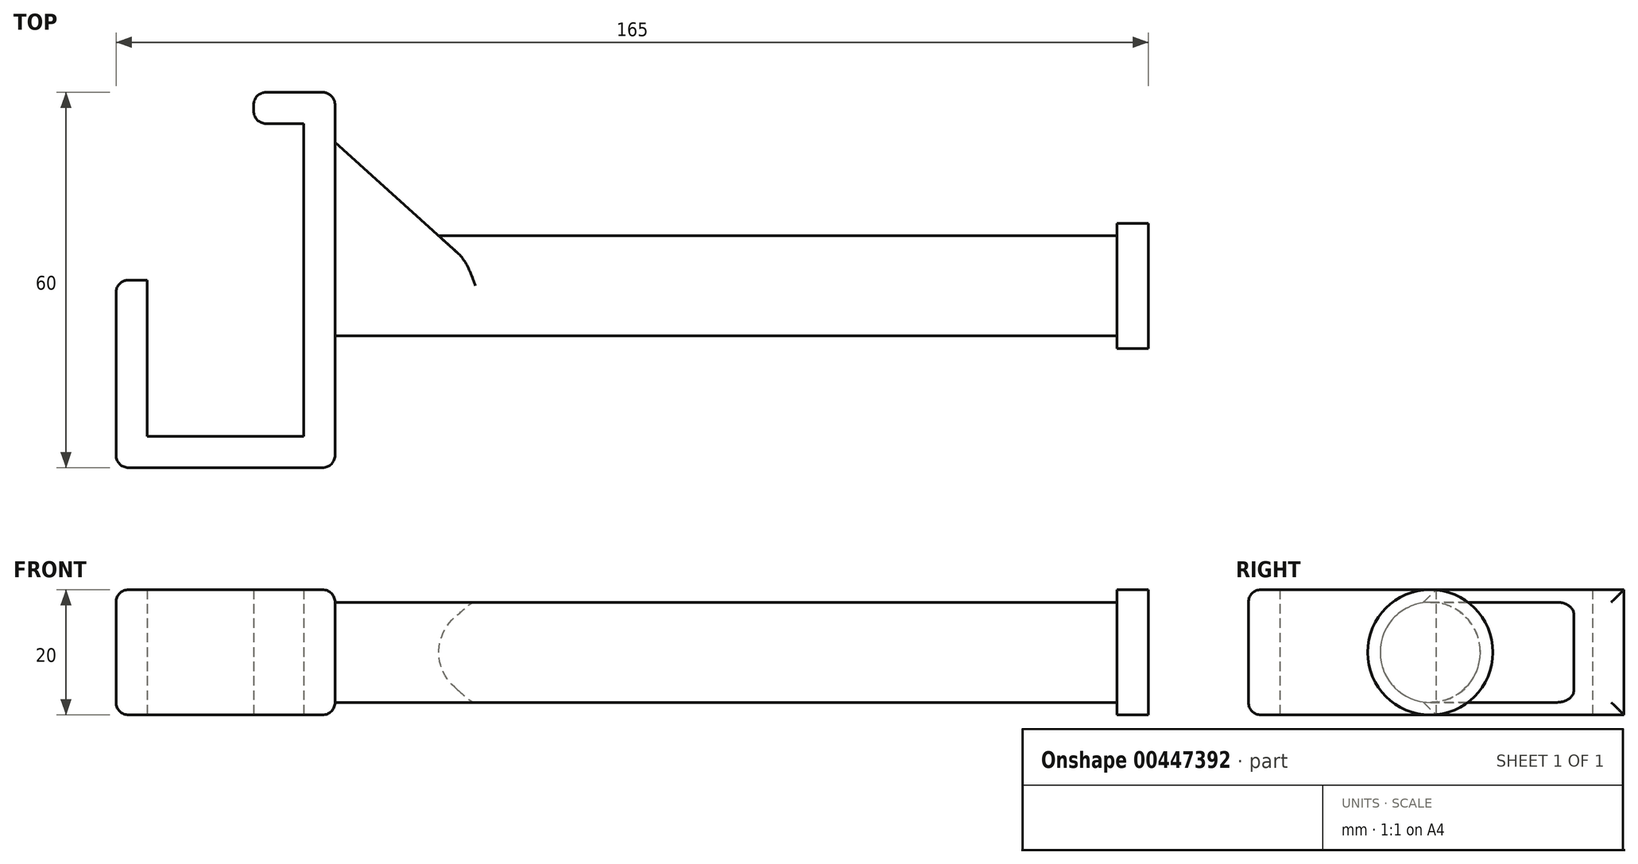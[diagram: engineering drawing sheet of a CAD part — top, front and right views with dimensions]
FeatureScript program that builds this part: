
annotation { "Feature Type Name" : "Feature", "Feature Type Description" : "" }
export const myFeature = defineFeature(function(context is Context, id is Id, definition is map)
    precondition{}
    {
        {
            var Q0;
            Q0=qCreatedBy(makeId("Top.planeOp"),FACE);
            var sketch = newSketch(context, id + "F0", { "sketchPlane" : qUnion([Q0])});
            skLineSegment(sketch, "E0", {"start": v(-33.28, 0.94) * mm, "end": v(-33.28, -24.06) * mm});
            skLineSegment(sketch, "E1", {"start": v(-33.28, -24.06) * mm, "end": v(-8.28, -24.06) * mm});
            skLineSegment(sketch, "E2", {"start": v(-8.28, -24.06) * mm, "end": v(-8.28, 25.94) * mm});
            skLineSegment(sketch, "E3", {"start": v(-8.28, 25.94) * mm, "end": v(-16.28, 25.94) * mm});
            skLineSegment(sketch, "E4.0", {"start": v(-3.28, 30.94) * mm, "end": v(-16.28, 30.94) * mm});
            skLineSegment(sketch, "E4.1", {"start": v(-3.28, -29.06) * mm, "end": v(-3.28, 30.94) * mm});
            skLineSegment(sketch, "E4.2", {"start": v(-38.28, -29.06) * mm, "end": v(-3.28, -29.06) * mm});
            skLineSegment(sketch, "E4.3", {"start": v(-38.28, 0.94) * mm, "end": v(-38.28, -29.06) * mm});
            skLineSegment(sketch, "E5", {"start": v(-16.28, 30.94) * mm, "end": v(-16.28, 25.94) * mm});
            skLineSegment(sketch, "E6", {"start": v(-38.28, 0.94) * mm, "end": v(-33.28, 0.94) * mm});
            skSolve(sketch);
        }
        {
            var Q0;
            Q0=makeQuery(id+"F0.imprint","IMPRINT",FACE,{"disambiguationData":[TD([[makeQuery(id+"F0.imprint","IMPRINT",EDGE,{"derivedFrom":sQuery(id+"F0.wireOp",EDGE,"E0")}),-1.0]])]});
            extrude(context, id + "F1", {"entities" : qUnion([Q0]), "endBound" : BoundingType.SYMMETRIC, "depth" : 20 * mm});
        }
        {
            var Q0;
            Q0=makeQuery(id+"F1.opExtrude","SWEPT_FACE",FACE,{"disambiguationData":[OSD([sQuery(id+"F0.wireOp",EDGE,"E4.1")])]});
            var sketch = newSketch(context, id + "F2", { "sketchPlane" : qUnion([Q0])});
            skCircle(sketch, "E7", {"center": v(0, 0) * mm, "radius": 8 * mm});
            skSolve(sketch);
        }
        {
            var Q0;
            {var subQ0=sQuery(id+"F2.wireOp",EDGE,"E7");var subQ1=sQuery(id+"F0.wireOp",EDGE,"E4.1");var subQ2=makeQuery(id+"F2.imprint","INTERSECT",VERTEX,{"derivedFrom":[makeQuery(id+"F1.opExtrude","CAP_EDGE",EDGE,{"disambiguationData":[OSD([subQ1])],"isStart":true}),subQ0]});Q0=makeQuery(id+"F2.imprint","IMPRINT",FACE,{"disambiguationData":[TD([[makeQuery(id+"F2.imprint","IMPRINT",EDGE,{"disambiguationData":[TD([[subQ2,1.0]])],"derivedFrom":subQ0}),1.0]])]});}
            extrude(context, id + "F3", {"entities" : qUnion([Q0]), "operationType" : NewBodyOperationType.ADD, "depth" : 125 * mm});
        }
        {
            var Q0;
            Q0=makeQuery(id+"F3.opExtrude","CAP_FACE",FACE,{"disambiguationData":[OSD([sQuery(id+"F2.wireOp",EDGE,"E7")])],"isStart":false});
            var sketch = newSketch(context, id + "F4", { "sketchPlane" : qUnion([Q0])});
            skCircle(sketch, "E8", {"center": v(0, 0) * mm, "radius": 10 * mm});
            skSolve(sketch);
        }
        {
            var Q0;
            Q0=makeQuery(id+"F4.imprint","IMPRINT",FACE,{"disambiguationData":[TD([[makeQuery(id+"F4.imprint","IMPRINT",EDGE,{"derivedFrom":sQuery(id+"F4.wireOp",EDGE,"E8")}),1.0]])]});
            var Q1;
            Q1=makeQuery(id+"F4.imprint","IMPRINT",FACE,{"disambiguationData":[TD([[makeQuery(id+"F4.imprint","IMPRINT",EDGE,{"derivedFrom":makeQuery(id+"F3.opExtrude","CAP_EDGE",EDGE,{"disambiguationData":[OSD([sQuery(id+"F2.wireOp",EDGE,"E7")])],"isStart":false})}),1.0]])]});
            extrude(context, id + "F5", {"entities" : qUnion([Q0, Q1]), "operationType" : NewBodyOperationType.ADD, "depth" : 5 * mm});
        }
        {
            var Q0;
            Q0=qCreatedBy(makeId("Top.planeOp"),FACE);
            var sketch = newSketch(context, id + "F6", { "sketchPlane" : qUnion([Q0])});
            skLineSegment(sketch, "E9", {"start": v(-4.72, 24.28) * mm, "end": v(22.16, 0) * mm});
            skLineSegment(sketch, "E10", {"start": v(22.16, 0) * mm, "end": v(-7.47, 0) * mm});
            skLineSegment(sketch, "E11", {"start": v(-7.47, 0) * mm, "end": v(-4.72, 24.28) * mm});
            skSolve(sketch);
        }
        {
            var Q0;
            Q0=makeQuery(id+"F6.imprint","IMPRINT",FACE,{"disambiguationData":[TD([[makeQuery(id+"F6.imprint","IMPRINT",EDGE,{"derivedFrom":sQuery(id+"F6.wireOp",EDGE,"E9")}),-1.0]])]});
            extrude(context, id + "F7", {"entities" : qUnion([Q0]), "operationType" : NewBodyOperationType.ADD, "endBound" : BoundingType.SYMMETRIC, "depth" : 16 * mm});
        }
        {
            var Q0;
            Q0=makeQuery(id+"F7.opExtrude","CAP_EDGE",EDGE,{"disambiguationData":[OSD([sQuery(id+"F6.wireOp",EDGE,"E9")])],"isStart":false});
            var Q1;
            Q1=makeQuery(id+"F7.opExtrude","CAP_EDGE",EDGE,{"disambiguationData":[OSD([sQuery(id+"F6.wireOp",EDGE,"E9")])],"isStart":true});
            fillet(context, id + "F8", {"entities" : qUnion([Q0, Q1]), "radius" : 2 * mm, "tangentPropagation" : true, "allowEdgeOverflow" : false});
        }
        {
            var Q0;
            Q0=makeQuery(id+"F1.opExtrude","CAP_EDGE",EDGE,{"disambiguationData":[OSD([sQuery(id+"F0.wireOp",EDGE,"E4.1")])],"isStart":false});
            var Q1;
            Q1=makeQuery(id+"F1.opExtrude","CAP_EDGE",EDGE,{"disambiguationData":[OSD([sQuery(id+"F0.wireOp",EDGE,"E4.1")])],"isStart":true});
            var Q2;
            Q2=makeQuery(id+"F1.opExtrude","CAP_EDGE",EDGE,{"disambiguationData":[OSD([sQuery(id+"F0.wireOp",EDGE,"E4.2")])],"isStart":false});
            var Q3;
            Q3=makeQuery(id+"F1.opExtrude","CAP_EDGE",EDGE,{"disambiguationData":[OSD([sQuery(id+"F0.wireOp",EDGE,"E4.2")])],"isStart":true});
            var Q4;
            Q4=makeQuery(id+"F1.opExtrude","CAP_EDGE",EDGE,{"disambiguationData":[OSD([sQuery(id+"F0.wireOp",EDGE,"E4.3")])],"isStart":false});
            var Q5;
            Q5=makeQuery(id+"F1.opExtrude","CAP_EDGE",EDGE,{"disambiguationData":[OSD([sQuery(id+"F0.wireOp",EDGE,"E4.3")])],"isStart":true});
            var Q6;
            Q6=makeQuery(id+"F1.opExtrude","SWEPT_EDGE",EDGE,{"disambiguationData":[OSD([sQuery(id+"F0.wireOp",EDGE,"E4.2"),sQuery(id+"F0.wireOp",EDGE,"E4.3")])]});
            var Q7;
            Q7=makeQuery(id+"F1.opExtrude","SWEPT_EDGE",EDGE,{"disambiguationData":[OSD([sQuery(id+"F0.wireOp",EDGE,"E4.3"),sQuery(id+"F0.wireOp",EDGE,"E6")])]});
            var Q8;
            Q8=makeQuery(id+"F1.opExtrude","SWEPT_EDGE",EDGE,{"disambiguationData":[OSD([sQuery(id+"F0.wireOp",EDGE,"E4.1"),sQuery(id+"F0.wireOp",EDGE,"E4.2")])]});
            var Q9;
            Q9=makeQuery(id+"F1.opExtrude","SWEPT_EDGE",EDGE,{"disambiguationData":[OSD([sQuery(id+"F0.wireOp",EDGE,"E4.0"),sQuery(id+"F0.wireOp",EDGE,"E4.1")])]});
            var Q10;
            Q10=makeQuery(id+"F1.opExtrude","SWEPT_EDGE",EDGE,{"disambiguationData":[OSD([sQuery(id+"F0.wireOp",EDGE,"E4.0"),sQuery(id+"F0.wireOp",EDGE,"E5")])]});
            var Q11;
            Q11=makeQuery(id+"F1.opExtrude","SWEPT_EDGE",EDGE,{"disambiguationData":[OSD([sQuery(id+"F0.wireOp",EDGE,"E3"),sQuery(id+"F0.wireOp",EDGE,"E5")])]});
            fillet(context, id + "F9", {"entities" : qUnion([Q0, Q1, Q2, Q3, Q4, Q5, Q6, Q7, Q8, Q9, Q10, Q11]), "radius" : 2 * mm, "tangentPropagation" : true, "allowEdgeOverflow" : false});
        }
    });
